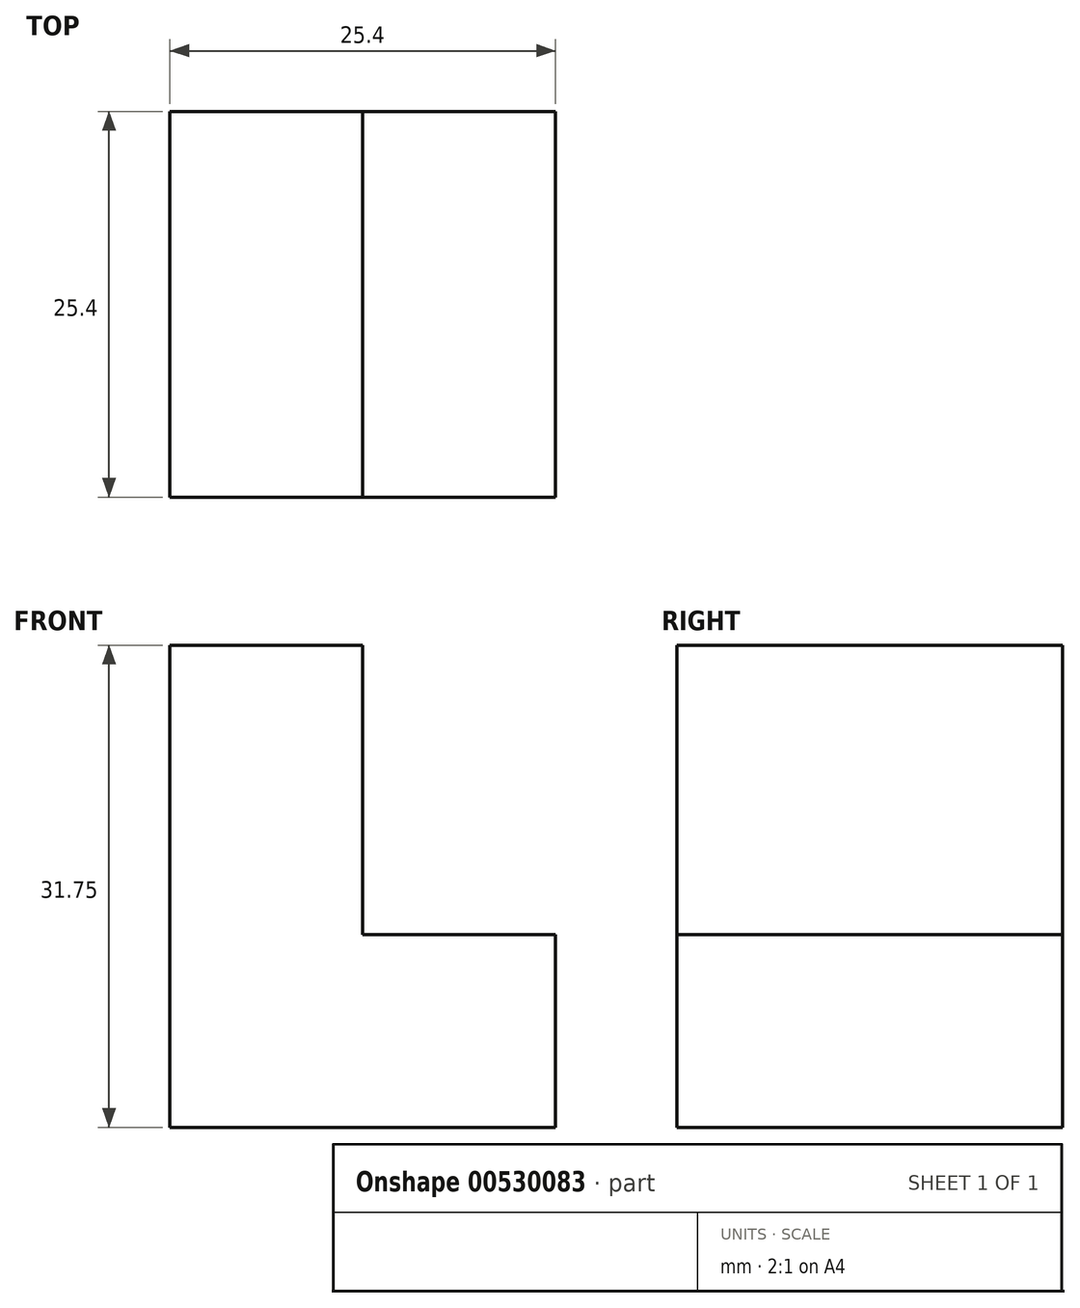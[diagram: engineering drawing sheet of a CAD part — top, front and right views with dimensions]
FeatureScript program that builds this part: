
annotation { "Feature Type Name" : "Feature", "Feature Type Description" : "" }
export const myFeature = defineFeature(function(context is Context, id is Id, definition is map)
    precondition{}
    {
        {
            var Q0;
            Q0=qCreatedBy(makeId("Front.planeOp"),FACE);
            var sketch = newSketch(context, id + "F0", { "sketchPlane" : qUnion([Q0])});
            skLineSegment(sketch, "E0", {"start": v(-55.5, 52.49) * mm, "end": v(-55.5, 20.74) * mm});
            skLineSegment(sketch, "E1", {"start": v(-55.5, 20.74) * mm, "end": v(-30.1, 20.74) * mm});
            skLineSegment(sketch, "E2", {"start": v(-30.1, 20.74) * mm, "end": v(-30.1, 33.44) * mm});
            skLineSegment(sketch, "E3", {"start": v(-30.1, 33.44) * mm, "end": v(-42.8, 33.44) * mm});
            skLineSegment(sketch, "E4", {"start": v(-42.8, 33.44) * mm, "end": v(-42.8, 52.49) * mm});
            skLineSegment(sketch, "E5", {"start": v(-55.5, 52.49) * mm, "end": v(-42.8, 52.49) * mm});
            skSolve(sketch);
        }
        {
            var Q0;
            Q0 = qSketchRegion(id + "F0", true);
            extrude(context, id + "F1", {"entities" : qUnion([Q0]), "depth" : 25.4 * mm, "offsetDistance" : 25.4 * mm});
        }
    });
